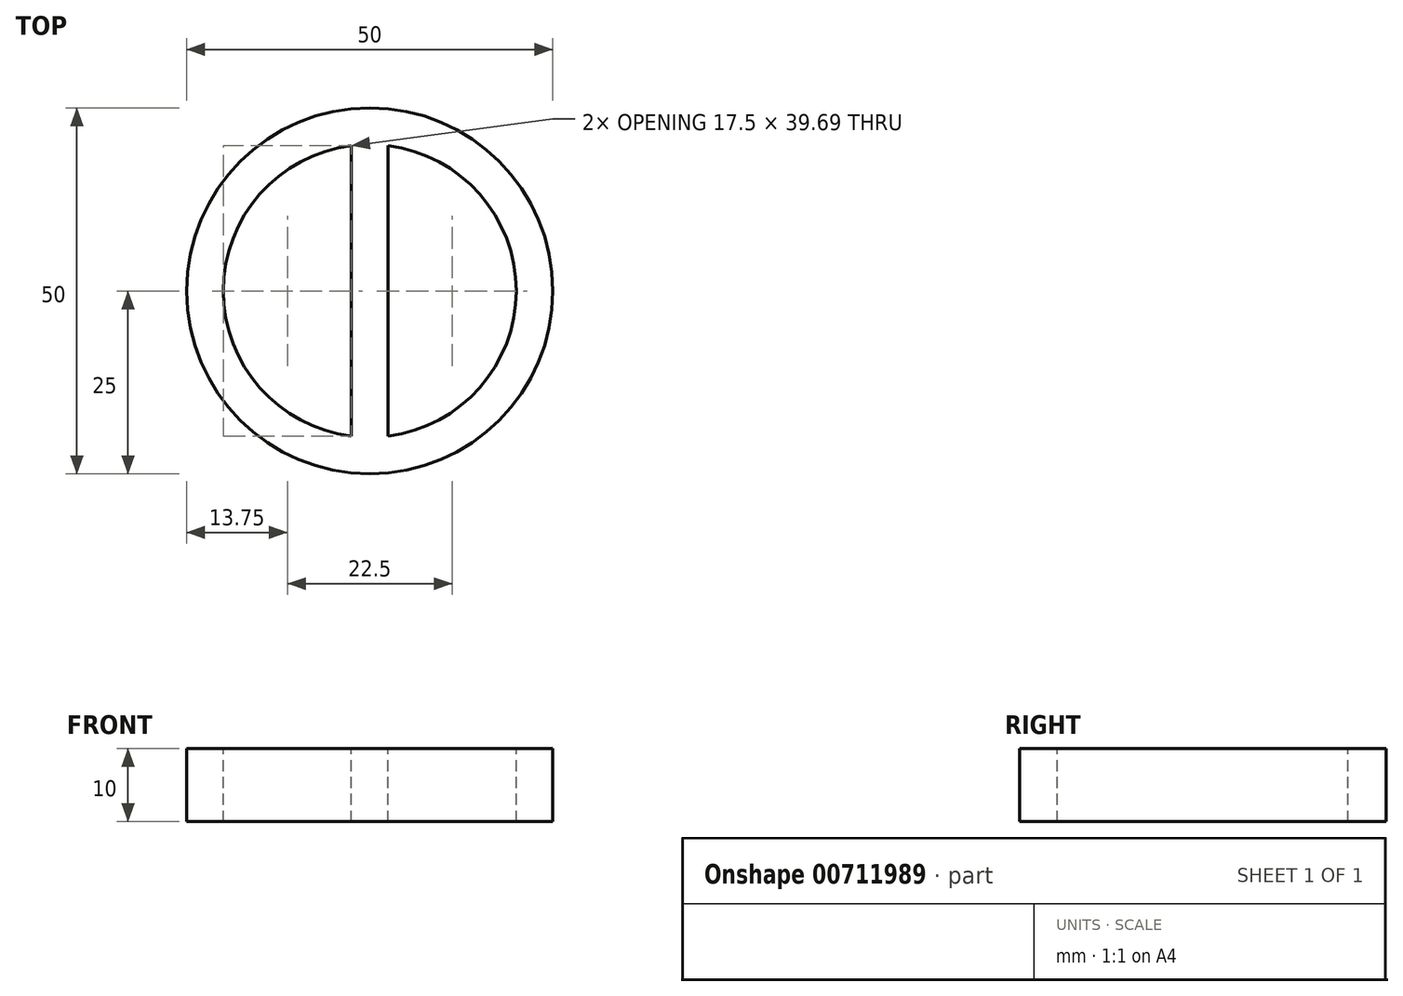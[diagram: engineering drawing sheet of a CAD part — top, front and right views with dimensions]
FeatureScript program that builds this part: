
annotation { "Feature Type Name" : "Feature", "Feature Type Description" : "" }
export const myFeature = defineFeature(function(context is Context, id is Id, definition is map)
    precondition{}
    {
        {
            var Q0;
            Q0=qCreatedBy(makeId("Top.planeOp"),FACE);
            var sketch = newSketch(context, id + "F0", { "sketchPlane" : qUnion([Q0])});
            skCircle(sketch, "E0", {"center": v(0, 0) * mm, "radius": 25 * mm});
            skSolve(sketch);
        }
        {
            var Q0;
            Q0 = qSketchRegion(id + "F0", true);
            extrude(context, id + "F1", {"entities" : qUnion([Q0]), "depth" : 10 * mm, "offsetDistance" : 25 * mm});
        }
        {
            var Q0;
            Q0=makeQuery(id+"F1.opExtrude","CAP_FACE",FACE,{"disambiguationData":[OSD([sQuery(id+"F0.wireOp",EDGE,"E0")])],"isStart":false});
            var sketch = newSketch(context, id + "F2", { "sketchPlane" : qUnion([Q0])});
            skLineSegment(sketch, "E1", {"start": v(-2.5, -19.84) * mm, "end": v(-2.5, 19.84) * mm});
            skArc(sketch, "E2", {"start": v(-2.5, 19.84) * mm, "mid": v(-20, 0) * mm, "end": v(-2.5, -19.84) * mm});
            skLineSegment(sketch, "E3.1.0", {"start": v(2.5, 19.84) * mm, "end": v(2.5, -19.84) * mm});
            skArc(sketch, "E3.1.1", {"start": v(2.5, -19.84) * mm, "mid": v(20, 0) * mm, "end": v(2.5, 19.84) * mm});
            skSolve(sketch);
        }
        {
            var Q0;
            Q0 = qSketchRegion(id + "F2", true);
            extrude(context, id + "F3", {"entities" : qUnion([Q0]), "operationType" : NewBodyOperationType.REMOVE, "oppositeDirection" : true, "depth" : 10 * mm, "offsetDistance" : 25 * mm});
        }
    });
